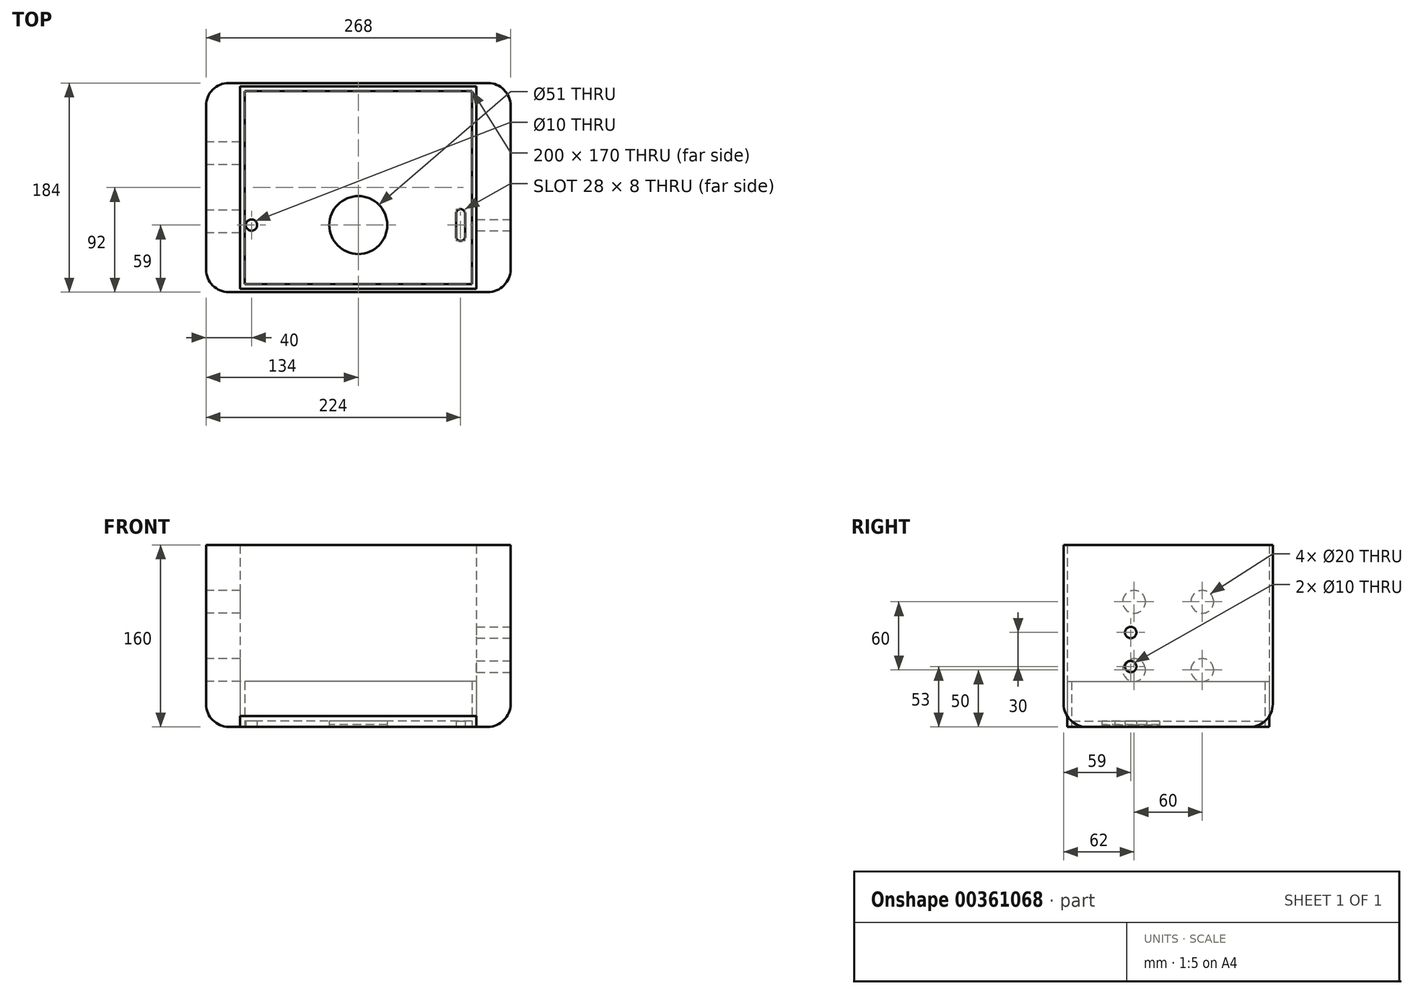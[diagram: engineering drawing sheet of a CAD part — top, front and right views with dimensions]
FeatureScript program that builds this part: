
annotation { "Feature Type Name" : "Feature", "Feature Type Description" : "" }
export const myFeature = defineFeature(function(context is Context, id is Id, definition is map)
    precondition{}
    {
        {
            var Q0;
            Q0=qCreatedBy(makeId("Top.planeOp"),FACE);
            var sketch = newSketch(context, id + "F0", { "sketchPlane" : qUnion([Q0])});
            skLineSegment(sketch, "E0.bottom", {"start": v(134, -59) * mm, "end": v(-134, -59) * mm});
            skLineSegment(sketch, "E0.top", {"start": v(134, 125) * mm, "end": v(-134, 125) * mm});
            skPoint(sketch, "E0.middle", {"position": v(0, 0) * mm});
            skCircle(sketch, "E1", {"center": v(0, 0) * mm, "radius": 25.5 * mm});
            skLineSegment(sketch, "E2.0", {"start": v(-100, -52) * mm, "end": v(-100, 118) * mm});
            skLineSegment(sketch, "E2.1", {"start": v(100, -52) * mm, "end": v(-100, -52) * mm});
            skLineSegment(sketch, "E2.2", {"start": v(100, -52) * mm, "end": v(100, 118) * mm});
            skLineSegment(sketch, "E2.3", {"start": v(100, 118) * mm, "end": v(-100, 118) * mm});
            skLineSegment(sketch, "E3.0", {"start": v(104, 122) * mm, "end": v(-104, 122) * mm});
            skLineSegment(sketch, "E3.1", {"start": v(104, -56) * mm, "end": v(104, 122) * mm});
            skLineSegment(sketch, "E3.2", {"start": v(104, -56) * mm, "end": v(-104, -56) * mm});
            skLineSegment(sketch, "E3.3", {"start": v(-104, -56) * mm, "end": v(-104, 122) * mm});
            skLineSegment(sketch, "E4", {"start": v(134, -59) * mm, "end": v(134, 125) * mm});
            skPoint(sketch, "E5.endSnap0", {"position": v(134, 33) * mm});
            skLineSegment(sketch, "E6", {"start": v(94, 0) * mm, "end": v(94, -10) * mm});
            skLineSegment(sketch, "E7", {"start": v(94, 0) * mm, "end": v(94, 10) * mm});
            skArc(sketch, "E8", {"start": v(94, -10) * mm, "mid": v(90, -14) * mm, "end": v(86, -10) * mm});
            skArc(sketch, "E9", {"start": v(94, 10) * mm, "mid": v(90, 14) * mm, "end": v(86, 10) * mm});
            skLineSegment(sketch, "E10", {"start": v(86, -10) * mm, "end": v(86, 10) * mm});
            skLineSegment(sketch, "E11", {"start": v(-134, 125) * mm, "end": v(-134, -59) * mm});
            skPoint(sketch, "E12", {"position": v(-94, 0) * mm});
            skCircle(sketch, "E13", {"center": v(-94, 0) * mm, "radius": 5 * mm});
            skSolve(sketch);
        }
        {
            var Q0;
            Q0=makeQuery(id+"F0.imprint","IMPRINT",FACE,{"disambiguationData":[TD([[makeQuery(id+"F0.imprint","IMPRINT",EDGE,{"derivedFrom":sQuery(id+"F0.wireOp",EDGE,"E1")}),1.0]])]});
            extrude(context, id + "F1", {"entities" : qUnion([Q0]), "depth" : 2 * mm});
        }
        {
            var Q0;
            Q0=makeQuery(id+"F0.imprint","IMPRINT",FACE,{"disambiguationData":[TD([[makeQuery(id+"F0.imprint","IMPRINT",EDGE,{"derivedFrom":sQuery(id+"F0.wireOp",EDGE,"E1")}),-1.0]])]});
            var Q1;
            Q1=makeQuery(id+"F0.imprint","IMPRINT",FACE,{"disambiguationData":[TD([[makeQuery(id+"F0.imprint","IMPRINT",EDGE,{"derivedFrom":sQuery(id+"F0.wireOp",EDGE,"wDK2D86D-5Smb-rO2F-uM56-sWFtckQkBcLd")}),1.0]])]});
            extrude(context, id + "F2", {"entities" : qUnion([Q0, Q1]), "depth" : 5 * mm});
        }
        {
            var Q0;
            {var subQ5=sQuery(id+"F0.wireOp",EDGE,"E0.bottom");Q0=makeQuery(id+"F0.imprint","IMPRINT",FACE,{"disambiguationData":[TD([[makeQuery(id+"F0.imprint","IMPRINT",EDGE,{"derivedFrom":subQ5}),-1.0]])]});}
            extrude(context, id + "F3", {"entities" : qUnion([Q0]), "depth" : 160 * mm});
        }
        {
            var Q0;
            Q0=makeQuery(id+"F0.imprint","IMPRINT",FACE,{"disambiguationData":[TD([[makeQuery(id+"F0.imprint","IMPRINT",EDGE,{"derivedFrom":sQuery(id+"F0.wireOp",EDGE,"E2.0")}),1.0]])]});
            extrude(context, id + "F4", {"entities" : qUnion([Q0]), "depth" : 40 * mm});
        }
        {
            var Q0;
            Q0=makeQuery(id+"F3.opExtrude","SWEPT_FACE",FACE,{"disambiguationData":[OSD([sQuery(id+"F0.wireOp",EDGE,"E4")])]});
            var sketch = newSketch(context, id + "F5", { "sketchPlane" : qUnion([Q0])});
            skLineSegment(sketch, "E14", {"start": v(33, 0) * mm, "end": v(33, 35) * mm});
            skLineSegment(sketch, "E15", {"start": v(33, 35) * mm, "end": v(33, 45) * mm});
            skPoint(sketch, "E16.middle", {"position": v(0, 53) * mm});
            skPoint(sketch, "E17.middle", {"position": v(0, 83) * mm});
            skCircle(sketch, "E18", {"center": v(0, 83) * mm, "radius": 5 * mm});
            skCircle(sketch, "E19", {"center": v(0, 53) * mm, "radius": 5 * mm});
            skSolve(sketch);
        }
        {
            var Q0;
            Q0=makeQuery(id+"F5.imprint","IMPRINT",FACE,{"disambiguationData":[TD([[makeQuery(id+"F5.imprint","IMPRINT",EDGE,{"derivedFrom":sQuery(id+"F5.wireOp",EDGE,"E18")}),1.0]])]});
            extrude(context, id + "F6", {"entities" : qUnion([Q0]), "operationType" : NewBodyOperationType.REMOVE, "oppositeDirection" : true, "depth" : 30.3 * mm});
        }
        {
            var Q0;
            Q0=makeQuery(id+"F5.imprint","IMPRINT",FACE,{"disambiguationData":[TD([[makeQuery(id+"F5.imprint","IMPRINT",EDGE,{"derivedFrom":sQuery(id+"F5.wireOp",EDGE,"E19")}),1.0]])]});
            extrude(context, id + "F7", {"entities" : qUnion([Q0]), "operationType" : NewBodyOperationType.REMOVE, "oppositeDirection" : true, "depth" : 30 * mm});
        }
        {
            var Q0;
            Q0=makeQuery(id+"F0.imprint","IMPRINT",FACE,{"disambiguationData":[TD([[makeQuery(id+"F0.imprint","IMPRINT",EDGE,{"derivedFrom":sQuery(id+"F0.wireOp",EDGE,"E6")}),-1.0]])]});
            extrude(context, id + "F8", {"entities" : qUnion([Q0]), "operationType" : NewBodyOperationType.REMOVE, "depth" : 10 * mm});
        }
        {
            var Q0;
            Q0=makeQuery(id+"F3.opExtrude","SWEPT_FACE",FACE,{"disambiguationData":[OSD([sQuery(id+"F0.wireOp",EDGE,"E11")])]});
            var sketch = newSketch(context, id + "F9", { "sketchPlane" : qUnion([Q0])});
            skLineSegment(sketch, "E20", {"start": v(-33, 0) * mm, "end": v(-33, 160) * mm, "construction": true});
            skLineSegment(sketch, "E21", {"start": v(-125, 80) * mm, "end": v(59, 80) * mm, "construction": true});
            skPoint(sketch, "E22", {"position": v(-33, 80) * mm});
            skPoint(sketch, "E23", {"position": v(-33, 110) * mm});
            skPoint(sketch, "E24", {"position": v(-33, 50) * mm});
            skPoint(sketch, "E25", {"position": v(-3, 80) * mm});
            skPoint(sketch, "E26", {"position": v(-63, 80) * mm});
            skCircle(sketch, "E27", {"center": v(-3, 50) * mm, "radius": 10 * mm});
            skCircle(sketch, "E28", {"center": v(-63, 50) * mm, "radius": 10 * mm});
            skCircle(sketch, "E29", {"center": v(-63, 110) * mm, "radius": 10 * mm});
            skCircle(sketch, "E30", {"center": v(-3, 110) * mm, "radius": 10 * mm});
            skSolve(sketch);
        }
        {
            var Q0;
            Q0=makeQuery(id+"F9.imprint","IMPRINT",FACE,{"disambiguationData":[TD([[makeQuery(id+"F9.imprint","IMPRINT",EDGE,{"derivedFrom":sQuery(id+"F9.wireOp",EDGE,"E29")}),1.0]])]});
            var Q1;
            Q1=makeQuery(id+"F9.imprint","IMPRINT",FACE,{"disambiguationData":[TD([[makeQuery(id+"F9.imprint","IMPRINT",EDGE,{"derivedFrom":sQuery(id+"F9.wireOp",EDGE,"E30")}),1.0]])]});
            var Q2;
            Q2=makeQuery(id+"F9.imprint","IMPRINT",FACE,{"disambiguationData":[TD([[makeQuery(id+"F9.imprint","IMPRINT",EDGE,{"derivedFrom":sQuery(id+"F9.wireOp",EDGE,"E28")}),1.0]])]});
            var Q3;
            Q3=makeQuery(id+"F9.imprint","IMPRINT",FACE,{"disambiguationData":[TD([[makeQuery(id+"F9.imprint","IMPRINT",EDGE,{"derivedFrom":sQuery(id+"F9.wireOp",EDGE,"E27")}),1.0]])]});
            var Q4;
            Q4=makeQuery(id+"F3.opExtrude","SWEPT_FACE",FACE,{"disambiguationData":[OSD([sQuery(id+"F0.wireOp",EDGE,"E3.3")])]});
            extrude(context, id + "F10", {"entities" : qUnion([Q0, Q1, Q2, Q3]), "operationType" : NewBodyOperationType.REMOVE, "endBound" : BoundingType.UP_TO_SURFACE, "oppositeDirection" : true, "endBoundEntityFace" : qUnion([Q4]), "depth" : 25 * mm});
        }
        {
            var Q0;
            Q0=makeQuery(id+"F3.opExtrude","SWEPT_EDGE",EDGE,{"disambiguationData":[OSD([sQuery(id+"F0.wireOp",EDGE,"E0.bottom"),sQuery(id+"F0.wireOp",EDGE,"E11")])]});
            var Q1;
            Q1=makeQuery(id+"F3.opExtrude","SWEPT_EDGE",EDGE,{"disambiguationData":[OSD([sQuery(id+"F0.wireOp",EDGE,"E0.top"),sQuery(id+"F0.wireOp",EDGE,"E11")])]});
            var Q2;
            Q2=makeQuery(id+"F3.opExtrude","CAP_EDGE",EDGE,{"disambiguationData":[OSD([sQuery(id+"F0.wireOp",EDGE,"E4")])],"isStart":true});
            var Q3;
            Q3=makeQuery(id+"F3.opExtrude","SWEPT_EDGE",EDGE,{"disambiguationData":[OSD([sQuery(id+"F0.wireOp",EDGE,"E0.bottom"),sQuery(id+"F0.wireOp",EDGE,"E4")])]});
            var Q4;
            Q4=makeQuery(id+"F3.opExtrude","CAP_EDGE",EDGE,{"disambiguationData":[OSD([sQuery(id+"F0.wireOp",EDGE,"E0.bottom")])],"isStart":true});
            var Q5;
            Q5=makeQuery(id+"F3.opExtrude","CAP_EDGE",EDGE,{"disambiguationData":[OSD([sQuery(id+"F0.wireOp",EDGE,"E0.top")])],"isStart":true});
            var Q6;
            Q6=makeQuery(id+"F3.opExtrude","CAP_EDGE",EDGE,{"disambiguationData":[OSD([sQuery(id+"F0.wireOp",EDGE,"E11")])],"isStart":true});
            var Q7;
            Q7=makeQuery(id+"F3.opExtrude","SWEPT_EDGE",EDGE,{"disambiguationData":[OSD([sQuery(id+"F0.wireOp",EDGE,"E0.top"),sQuery(id+"F0.wireOp",EDGE,"E4")])]});
            fillet(context, id + "F11", {"entities" : qUnion([Q0, Q1, Q2, Q3, Q4, Q5, Q6, Q7]), "radius" : 20 * mm, "tangentPropagation" : true, "allowEdgeOverflow" : false});
        }
    });
